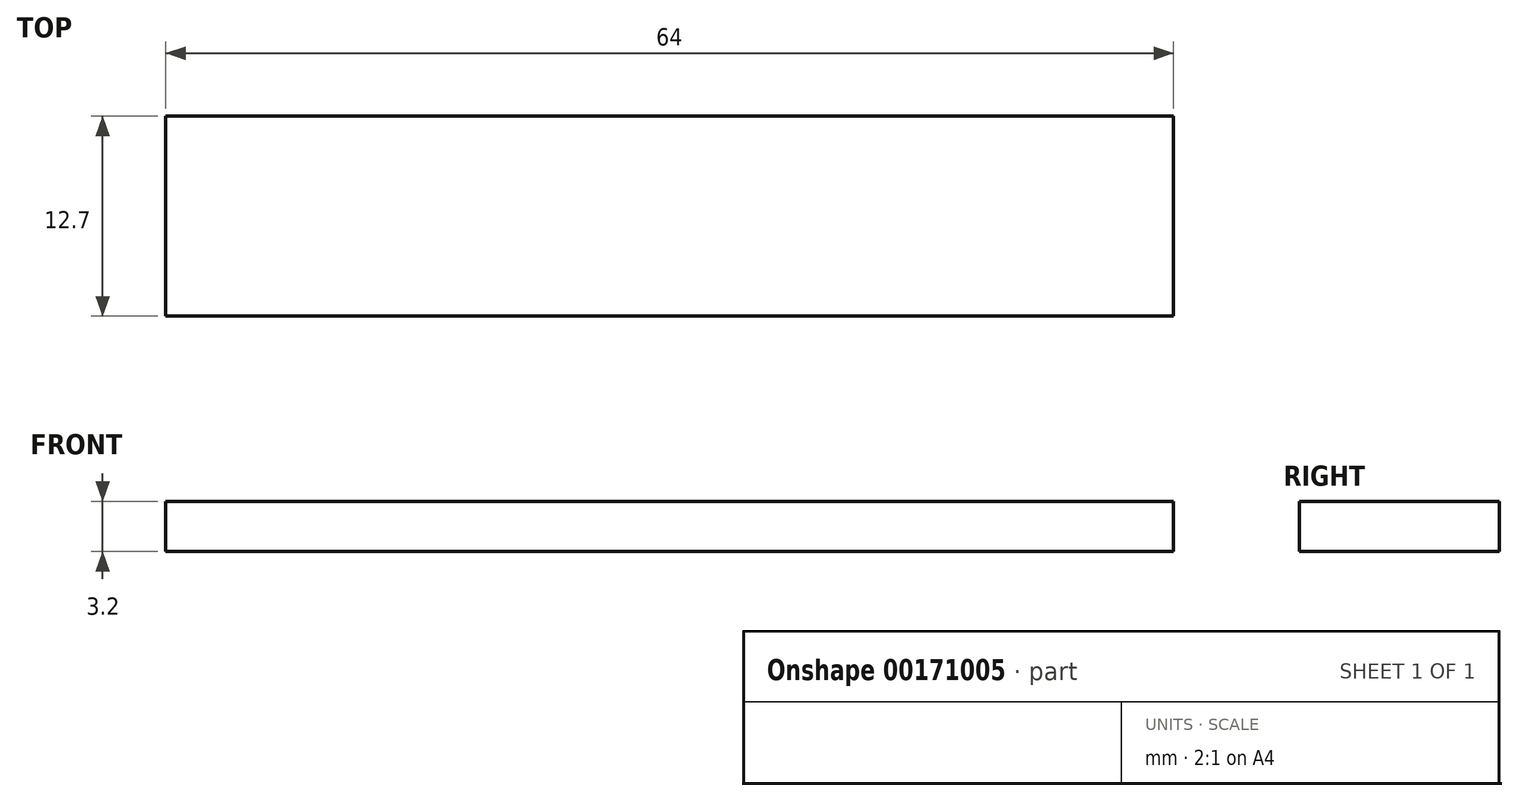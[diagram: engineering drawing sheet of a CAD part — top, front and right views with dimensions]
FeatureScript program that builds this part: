
annotation { "Feature Type Name" : "Feature", "Feature Type Description" : "" }
export const myFeature = defineFeature(function(context is Context, id is Id, definition is map)
    precondition{}
    {
        {
            var Q0;
            Q0=qCreatedBy(makeId("Top.planeOp"),FACE);
            var sketch = newSketch(context, id + "F0", { "sketchPlane" : qUnion([Q0])});
            skLineSegment(sketch, "E0.bottom", {"start": v(32, -6.35) * mm, "end": v(-32, -6.35) * mm});
            skLineSegment(sketch, "E0.top", {"start": v(32, 6.35) * mm, "end": v(-32, 6.35) * mm});
            skLineSegment(sketch, "E0.left", {"start": v(32, -6.35) * mm, "end": v(32, 6.35) * mm});
            skLineSegment(sketch, "E0.right", {"start": v(-32, -6.35) * mm, "end": v(-32, 6.35) * mm});
            skPoint(sketch, "E0.middle", {"position": v(0, 0) * mm});
            skSolve(sketch);
        }
        {
            var Q0;
            Q0=makeQuery(id+"F0.imprint","IMPRINT",FACE,{"disambiguationData":[TD([[makeQuery(id+"F0.imprint","IMPRINT",EDGE,{"derivedFrom":sQuery(id+"F0.wireOp",EDGE,"E0.bottom")}),-1.0]])]});
            extrude(context, id + "F1", {"entities" : qUnion([Q0]), "depth" : 3.2 * mm});
        }
    });
